# Revit family: QF_ELECTROLUXPROFESSIONAL_1LSN93_WH6-11_E
name_source: partatom
category: Attrezzature speciali
units: mm (PartAtom-declared; Revit-internal decimal feet)

## family parameters
Basato su piano di lavoro = No
Condiviso = No
Punto di calcolo locali = No
Quota connettore circolare = Usa diametro
Sempre verticale = Sì
Taglio con vuoti quando caricato = No
Tipo di parte = Normale

## types (43) — shared parameters
Depth Actual = 766 mm  [stored 2.51312 ft]
Height Actual = 1212 mm  [stored 3.97638 ft]
Latent Heat Output = 0.0
Length Actual = 830 mm  [stored 2.7231 ft]
Modello = WH6-11
Produttore = Electrolux Professional
Sensible Heat Output = 0.0
URL = www.electroluxprofessional.com
Weight = 202
zero-valued in all types: Gas KW, Prospetto di default, Steam Pounds per Hour

## per-type parameters (varying)
| type | Cycle | Descrizione | Item Number | Phase | Volts | Watts |
| 9867730102 | 60 Hz | WASHER WH6-11 11KG EL 10KW 220-240/60/3 COMPASS PRO 6G01 ML 2xWATER POWDER+5xLIQ. EL.VALV.OPEN SILVER 2.I/O DISCON. STOP | 1L8242 | 3 | 240 V | 10100 W |
| 9867730260 | 60 Hz | WASHER WH6-11 11KG NO HEAT 208-240/60/1 COMPASS PRO 6G01 ML 2xWATER POWDER+5xLIQ. VALV.OPEN SILVER 2.I/O STOP | 1L0HED | 1 | 240 V | 1100 W |
| 9867730073 | 50 Hz | WASHER WH6-11 11KG EL 10KW 220-240/50/3 COMPASS PRO 6A01 ML 2xWATER POWDER+5xLIQ. VALV.OPEN SILVER 2.I/O DISCON. | 1L0G8R | 3 | 240 V | 10100 W |
| 9867730200 | 50 Hz | WASHER WH6-11 11KG MOP 10KW 380-415/50/3 COMPASS PRO 6M14 ML 2xWATER POWDER+5xLIQ. EL.VALV.OPEN SILVER 2.I/O TRAFO DISCO | 1LSNGS | 3 | 415 V | 10100 W |
| 9867730086 | 50 Hz | WASHER WH6-11 11KG MOP 10KW 380-415/220-240/50/3N/3 COMPASS PRO 6M14 ML 2xWATER POWDER+5xLIQ. EL.VALV.OPEN SILVER 2.I/O | 1L823X | 3 | 415 V | 10100 W |
| 9867730220 | 50 Hz | WASHER WH6-11 11KG NO HEAT 220-240/50/1N COMPASS PRO 6L01 ML 2xWATER 5xLIQ. VALV.OPEN SILVER 2.I/O DISCON. | 1LSPR9 | 1 | 240 V | 1100 W |
| 9867730248 | 50 Hz | WASHER WH6-11 11KG EL 10KW 380-415/50/3 COMPASS PRO 6G01 ML 2xWATER POWDER+5xLIQ. VALV.OPEN SILVER 2.I/O TRAFO DISCON. S | 1L0HDP | 3 | 415 V | 8400 W |
| 9867730026 | 50 Hz | WASHER WH6-11 11KG EL 10KW 380-415/50/3N COMPASS PRO 6G01 ML 2xWATER POWDER+5xLIQ. VALV.OPEN SILVER 2.I/O DISCON. STOP | 1L0G8J | 3 | 415 V | 10100 W |
| 9867730228 | 60 Hz | WASHER WH6-11 11KG MOP 10KW 380-415/220-240/60/3N/3 COMPASS PRO 6M14 KR,EN 2xWATER POWDER+5xLIQ. EL.VALV.OPEN SST/SILVER | 1L0H2S | 3 | 415 V | 10100 W |
| 9867730253 | 50 Hz | WASHER WH6-11 11KG EL 10KW 380-415/50/3N COMPASS PRO 6A01 ML 2xWATER POWDER+5xLIQ. VALV.OPEN SILVER ELS-NETW. 2.I/O DISC | 1L82CP | 3 | 415 V | 8400 W |
| 9867730104 | 50 Hz | WASHER WH6-11 11KG MOP 10KW 380-415/220-240/50/3N/3 COMPASS PRO 6M17 ML 2xWATER POWDER+5xLIQ. EL.VALV.CLOSED SILVER 2.I/ | 1L0GAC | 3 | 415 V | 10100 W |
| 9867730085 | 50 Hz | WASHER WH6-11 11KG MOP 10KW 380-415/220-240/50/3N/3 COMPASS PRO 6M16 ML 2xWATER POWDER+5xLIQ. EL.VALV.CLOSED SILVER 2.I/ | 1L823W | 3 | 415 V | 10100 W |
| 9867730124 | 50 Hz | WASHER WH6-11 11KG EL 10KW 380-415/50/3N COMPASS PRO 6A01 SE 2xWATER POWDER+5xLIQ. VALV.OPEN SILVER PREP.CB INS. 2.I/O D | 1LA1CU | 3 | 415 V | 10100 W |
| 9867730151 | 50 Hz | WASHER WH6-11 11KG EL 7,5KW 380-415/50/3N COMPASS PRO 6G01 ML 2xWATER POWDER+5xLIQ. VALV.OPEN SILVER 2.I/O DISCON. STOP | 1L0GJ3 | 3 | 415 V | 10100 W |
| 9867730171 | 50 Hz | WASHER WH6-11 11KG EL 7KW 200/50/60/3 COMPASS PRO 6H43 JP,EN 2xWATER POWDER+5xLIQ. VALV.OPEN SILVER 2.I/O DISCON. | 1L0GRG | 3 | 200 V | 7000 W |
| 9867730199 | 60 Hz | WASHER WH6-11 11KG EL 10KW 440/60/3 COMPASS PRO 6G07 ML 2xWATER POWDER+5xLIQ. VALV.OPEN SILVER 2.I/O TRAFO DISCON. STOP | 1L8281 | 3 | 440 V | 10100 W |
| 9867730119 | 50 Hz | WASHER WH6-11 11KG MOP 10KW 380-415/220-240/50/3N/3 COMPASS PRO 6M17 ML 2xWATER POWDER+5xLIQ. EL.VALV.CLOSED SILVER 2.I/ | 1LA1CR | 3 | 415 V | 10100 W |
| 9867730109 | 50 Hz | WASHER WH6-11 11KG EL 10KW 380-415/220-240/50/3N/3 COMPASS PRO 6H12 ML 2xWATER POWDER+5xLIQ. VALV.OPEN SILVER 2.I/O QC D | 1L0GBL | 3 | 415 V | 10100 W |
| 9867730201 | 60 Hz | WASHER WH6-11 11KG EL 7,5KW 440/60/3 COMPASS PRO 6G01 ML 2xWATER POWDER+5xLIQ. VALV.OPEN SILVER 2.I/O TRAFO DISCON. STOP | 1L828C | 3 | 440 V | 7600 W |
| 9867730088 | 50 Hz | WASHER WH6-11 11KG MOP 10KW 220-230/50/3 COMPASS PRO 6M14 ML 2xWATER POWDER+5xLIQ. EL.VALV.OPEN SILVER 2.I/O QC DISCON. | 1L823Z | 3 | 240 V | 10100 W |
| 9867730087 | 50 Hz | WASHER WH6-11 11KG MOP 10KW 380-400/220-230/50/3N/3 COMPASS PRO 6M14 ML 2xWATER POWDER+5xLIQ. EL.VALV.OPEN SILVER INS. 2 | 1L823Y | 3 | 415 V | 10100 W |
| 9867730221 | 50 Hz | WASHER WH6-11 11KG NO HEAT 220-240/50/1N COMPASS PRO 6L07 ML 2xWATER 5xLIQ. VALV.OPEN SILVER 2.I/O DISCON. | 1LSPRH | 1 | 240 V | 1100 W |
| 9867730058 | 50 Hz | WASHER WH6-11 11KG EL 10KW 380-415/50/3N COMPASS PRO 6H12 SE 2xWATER POWDER+5xLIQ. VALV.OPEN SILVER 2.I/O QC STOP | 1L824A | 3 | 415 V | 10100 W |
| 9867730057 | 50 Hz | WASHER WH6-11 11KG EL 10KW 380-415/50/3N COMPASS PRO 6A01 SE 2xWATER POWDER VALV.OPEN SILVER INS. DISCON. | 1L0G8N | 3 | 415 V | 10100 W |
| 9867730254 | 50 Hz | WASHER WH6-11 11KG EL 10KW 380-415/50/3 COMPASS PRO 6G07 CH-EN 2xWATER POWDER VALV.OPEN SILVER TRAFO DISCON. STOP | 1L82CW | 3 | 415 V | 8400 W |
| 9867730261 | 50 Hz | WASHER WH6-11 11KG EL 10KW 380-415/50/3 COMPASS PRO 6H01 ML 2xWATER POWDER+5xLIQ. VALV.OPEN SST/SILVER 2.I/O TRAFO DISCO | 1LT6A5 | 3 | 415 V | 8400 W |
| 9867730269 | 50 Hz | WH6-11 SS/SS 10 380415 EX 6G01 | 1L82E3 | 3 | 415 V | 8400 W |
| 9867730028 | 50 Hz | WASHER WH6-11 11KG EL 10KW 380-415/50/3N COMPASS PRO 6A01 ML 2xWATER POWDER VALV.OPEN SILVER DISCON. | 1L0G8K | 3 | 415 V | 10100 W |
| 9867730027 | 50 Hz | WASHER WH6-11 11KG EL 10KW 380-415/50/3N COMPASS PRO 6G01 ML 2xWATER POWDER VALV.OPEN SILVER DISCON. STOP | 1L822W | 3 | 415 V | 10100 W |
| 9867730103 | 50 Hz | WASHER WH6-11 11KG EL 10KW 220-240/50/3 COMPASS PRO 6G01 ML 2xWATER POWDER+5xLIQ. EL.VALV.OPEN SILVER 2.I/O DISCON. STOP | 1L825C | 3 | 240 V | 10100 W |
| 9867730072 | 50 Hz | WASHER WH6-11 11KG NO HEAT 220-240/50/1N COMPASS PRO 6L01 ML 2xWATER POWDER+5xLIQ. VALV.OPEN SILVER EXT.PM. 2.I/O DISCON | 1LSP5G | 1 | 240 V | 1100 W |
| 9867730170 | 50 Hz | WASHER WH6-11 11KG EL 10KW 380-415/50/3 COMPASS PRO 6G01 CH-EN 2xWATER POWDER VALV.OPEN SST/SILVER TRAFO DISCON. STOP | 1L0GRF | 3 | 415 V | 10100 W |
| 9867730100 | 50 Hz | WASHER WH6-11 11KG EL 10KW 380-415/50/3N COMPASS PRO 6H01 ML 2xWATER POWDER+5xLIQ. VALV.OPEN SST/SILVER 2.I/O DISCON. ST | 1L821M | 3 | 415 V | 10100 W |
| 9867730175 | 60 Hz | WASHER WH6-11 11KG NO HEAT 208-240/60/1 COMPASS PRO 6G01 ML 2xWATER POWDER EL.VALV.OPEN SILVER STOP | 1L8267 | 1 | 240 V | 1100 W |
| 9867730071 | 50 Hz | WASHER WH6-11 11KG EL 10KW 380-415/220-240/50/3N/1 COMPASS PRO 6H01 ML 2xWATER POWDER+5xLIQ. EL.VALV.OPEN SILVER 2.I/O D | 1L824C | 3 | 415 V | 10100 W |
| 9867730168 | 60 Hz | WASHER WH6-11 11KG MOP 10KW 380-415/220-240/60/3N/3 COMPASS PRO 6M14 KR,EN 2xWATER POWDER+5xLIQ. EL.VALV.OPEN SILVER 2.I | 1L0GPR | 3 | 415 V | 10200 W |
| 9867730262 | 60 Hz | WASHER WH6-11 11KG EL 10KW 380-415/60/3N COMPASS PRO 6G07 ML 2xWATER POWDER+5xLIQ. VALV.OPEN SILVER 2.I/O DISCON. STOP | 1L82DD | 3 | 415 V | 8400 W |
| 9867730084 | 50 Hz | WASHER WH6-11 11KG EL 10KW 380-415/220-240/50/3N/3 COMPASS PRO 6L01 ML 2xWATER POWDER+5xLIQ. VALV.OPEN SILVER EXT.PM. 2. | 1L823V | 3 | 415 V | 10100 W |
| 9867730125 | 50 Hz | WASHER WH6-11 11KG EL 10KW 380-415/50/3N COMPASS PRO 6A01 SE 2xWATER POWDER+5xLIQ. VALV.OPEN SILVER ELS-NETW. INS. 2.I/O | 1LA1CV | 3 | 415 V | 10100 W |
| 9867730089 | 50 Hz | WASHER WH6-11 11KG EL 10KW 380-400/220-230/50/3N/3 COMPASS PRO 6G01 ML 2xWATER POWDER+5xLIQ. VALV.OPEN SILVER 2.I/O DISC | 1LSP3L | 3 | 415 V | 10100 W |
| 9867730148 | 60 Hz | WASHER WH6-11 11KG EL 10KW 220-240/60/1N COMPASS PRO 6G07 ML 2xWATER POWDER+5xLIQ. PUMP SILVER 2.I/O DISCON. STOP | 1LSPDF | 1 | 230 V | 10100 W |
| 9867730059 | 50 Hz | WASHER WH6-11 11KG EL 10KW 380-415/50/3N COMPASS PRO 6A01 ML 2xWATER 5xLIQ. VALV.OPEN SILVER ELS-NETW. INS. 2.I/O DISCON | 1L0G8P | 3 | 415 V | 10100 W |
| 9867730074 | 50 Hz | WASHER WH6-11 11KG EL 10KW 380-415/220-240/50/3N/1 COMPASS PRO 6G01 ML 2xWATER POWDER+5xLIQ. PUMP SILVER 2.I/O DISCON. S | 1LSP5H | 3 | 415 V | 10100 W |

note: [stored X ft] marks values corroborated as IEEE doubles in the binary element streams (Revit-internal decimal feet)

## geometry (parser evidence)
native form markers: Blend x4
no freeform markers — native parametric forms only
